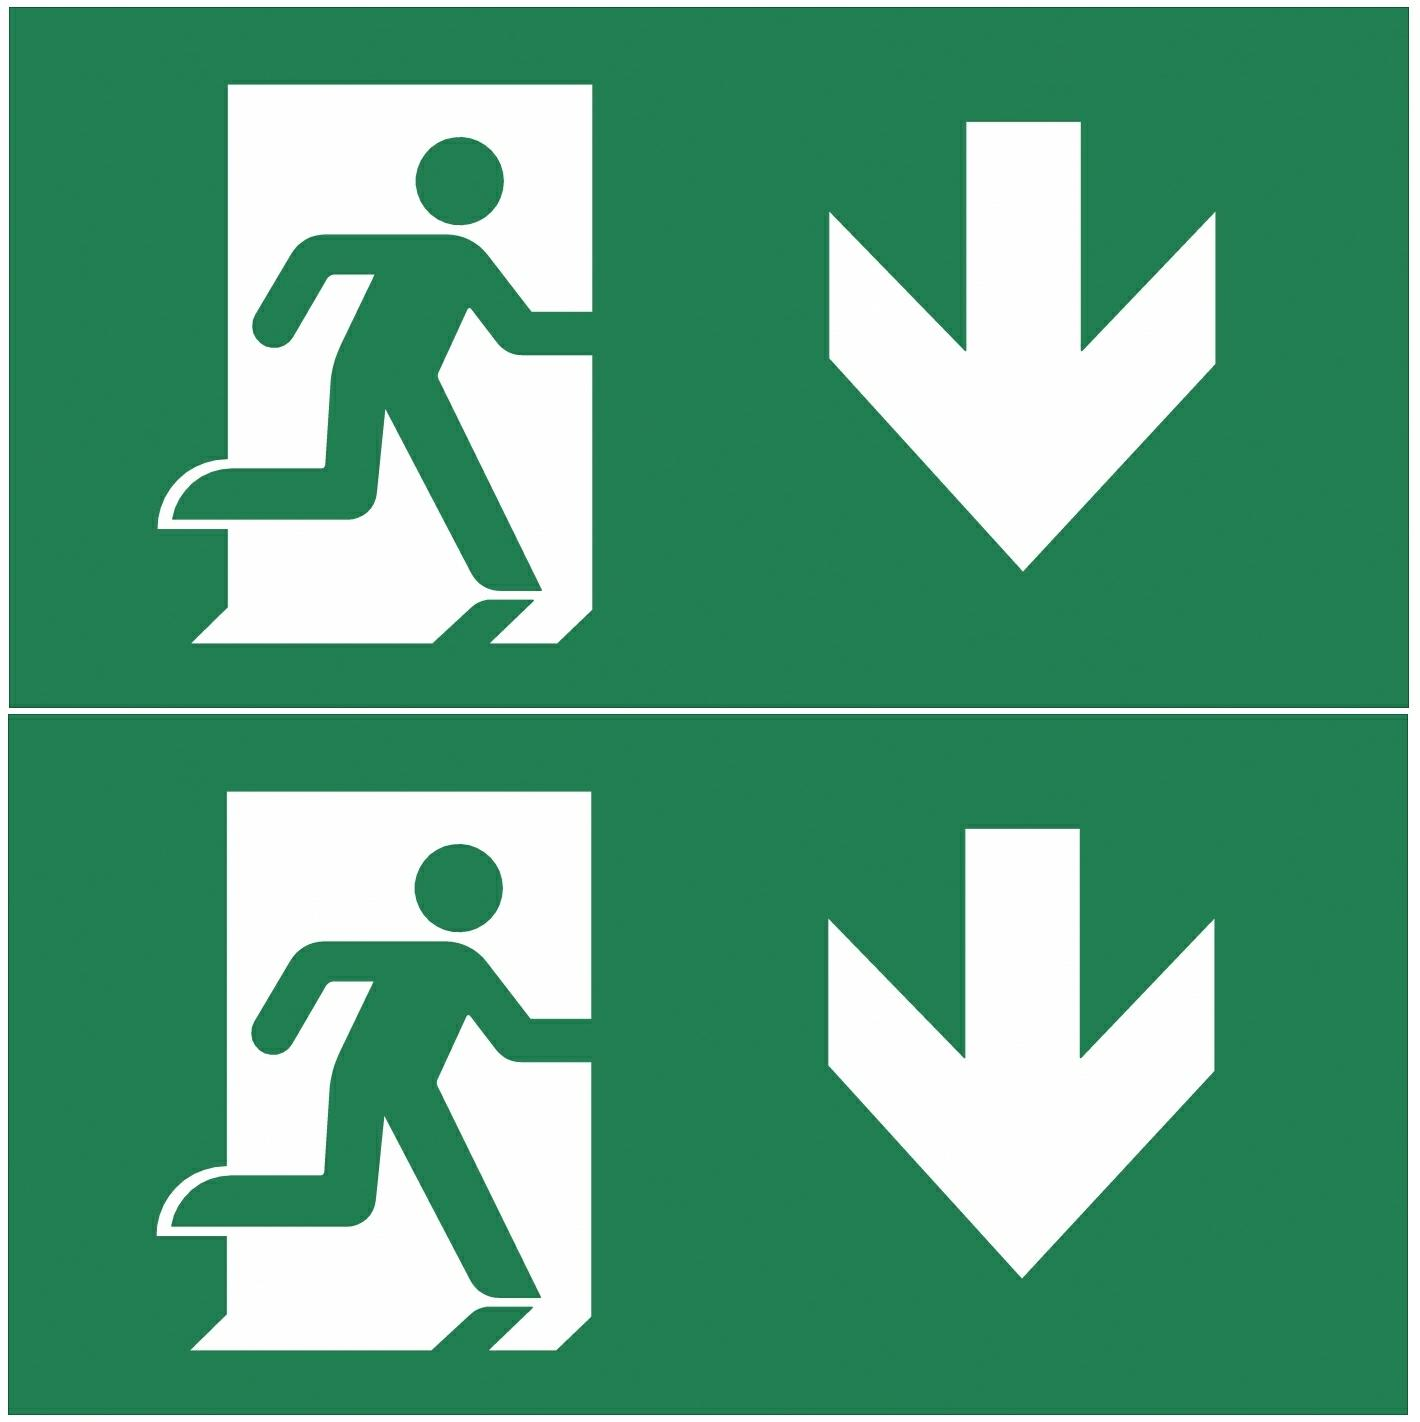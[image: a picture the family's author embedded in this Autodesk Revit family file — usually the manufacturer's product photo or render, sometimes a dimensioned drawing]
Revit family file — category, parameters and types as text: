
# Revit family: TWT8153WM
name_source: partatom
category: Lighting Fixtures
revit_build: Autodesk Revit 2016 (Build: 20150714_1515(x64)
units: mm (PartAtom-declared; Revit-internal decimal feet)

## family parameters
Always vertical = Yes
Cut with Voids When Loaded = No
Light Source = No
OmniClass Number = 23.80.70.00
OmniClass Title = Lighting
Part Type = Normal
Room Calculation Point = No
Round Connector Dimension = Use Diameter
Shared = No
Work Plane-Based = No

## types (4) — shared parameters
Aperture for Recess Mounting = 53 mm x 415 mm
Body Material = Plastic
Color = RAL9003
Customs Code = 94056080
Description = Self-Contained LED Exit Light with 1 h Battery Backup and Self Testing
ETIM Product Class = EC001957
Electrical Installation = 2/3 x 2,5 mm² -o-
Feature = Lumi Test
GTIN Code = 6438045011936
Glow Wire Test of Plastic Materials = 650 °C
Height = 287 mm
IP Class = IP44
Keynote = 23
Length = 408 mm
Light Source = LED
Manufacturer = Teknoware Oy
Max Input Power VA = 5 VA
Model = ESC 81
Mounting_Optional = Recess, Flag, Pendel
Mounting_Standard = Wall, Ceiling
Nominal Supply Voltage = 220-240 V, 50/60 Hz AC
Product Code = TWT8153WM
Protection Class = II
Sähkönumero = 4281017
Sähkönumerot.fi -tuotesivu = http://www.sahkonumerot.fi
Temperature Range Min_Max = -5...+30 °C
Type Image = ESC81.jpg
URL = http://www.teknoware.com
Viewing Distance = 60000 mm  [stored 196.85 ft]
Weight = 2.10 kg
Width = 40 mm  [stored 0.131234 ft]

## per-type parameters (varying)
| type | Max Input Power W | Pictogram Type |
| Arrow right_left 60m | 3 W | OPASTE PBV81601E |
| Arrow right_left 40m | 3 W | OPASTE PBV81401E |
| Arrow down 60m | 3 W | OPASTE PBV81602E |
| Arrow down 40m | 0 W | OPASTE PBV81402E |

note: [stored X ft] marks values corroborated as IEEE doubles in the binary element streams (Revit-internal decimal feet)

## geometry (parser evidence)
native form markers: Sweep x16
no freeform markers — native parametric forms only
